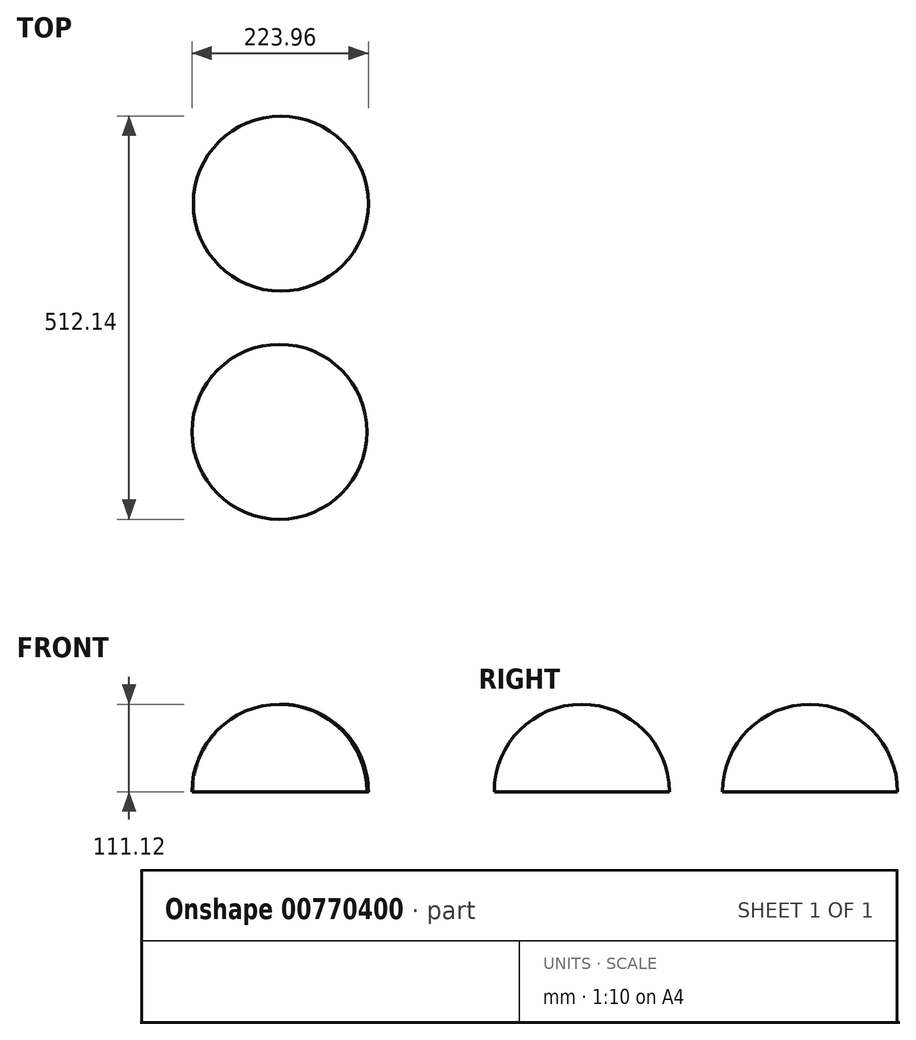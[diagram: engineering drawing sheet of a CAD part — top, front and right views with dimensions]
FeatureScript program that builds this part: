
annotation { "Feature Type Name" : "Feature", "Feature Type Description" : "" }
export const myFeature = defineFeature(function(context is Context, id is Id, definition is map)
    precondition{}
    {
        {
            var Q0;
            Q0=qCreatedBy(makeId("Top.planeOp"),FACE);
            var sketch = newSketch(context, id + "F0", { "sketchPlane" : qUnion([Q0])});
            skArc(sketch, "E0", {"start": v(7, 285.82) * mm, "mid": v(-87.3, 246.76) * mm, "end": v(-126.35, 152.47) * mm});
            skArc(sketch, "E1", {"start": v(-126.35, 152.47) * mm, "mid": v(-87.3, 58.18) * mm, "end": v(7, 19.12) * mm});
            skArc(sketch, "E2", {"start": v(7, 19.12) * mm, "mid": v(101.29, 58.18) * mm, "end": v(140.35, 152.47) * mm});
            skArc(sketch, "E3", {"start": v(140.35, 152.47) * mm, "mid": v(101.29, 246.76) * mm, "end": v(7, 285.82) * mm});
            skArc(sketch, "E4", {"start": v(7, 155.64) * mm, "mid": v(4.75, 154.71) * mm, "end": v(3.82, 152.47) * mm});
            skArc(sketch, "E5", {"start": v(3.82, 152.47) * mm, "mid": v(4.75, 150.22) * mm, "end": v(7, 149.3) * mm});
            skArc(sketch, "E6", {"start": v(7, 149.3) * mm, "mid": v(9.24, 150.22) * mm, "end": v(10.17, 152.47) * mm});
            skArc(sketch, "E7", {"start": v(10.17, 152.47) * mm, "mid": v(9.24, 154.71) * mm, "end": v(7, 155.64) * mm});
            skArc(sketch, "E8", {"start": v(5.29, -4.08) * mm, "mid": v(-89, -43.13) * mm, "end": v(-128.06, -137.43) * mm});
            skArc(sketch, "E9", {"start": v(-128.06, -137.43) * mm, "mid": v(-89, -231.72) * mm, "end": v(5.29, -270.78) * mm});
            skArc(sketch, "E10", {"start": v(5.29, -270.78) * mm, "mid": v(99.58, -231.72) * mm, "end": v(138.64, -137.43) * mm});
            skArc(sketch, "E11", {"start": v(138.64, -137.43) * mm, "mid": v(99.58, -43.13) * mm, "end": v(5.29, -4.08) * mm});
            skArc(sketch, "E12", {"start": v(5.29, -134.25) * mm, "mid": v(3.04, -135.18) * mm, "end": v(2.11, -137.43) * mm});
            skArc(sketch, "E13", {"start": v(2.11, -137.43) * mm, "mid": v(3.04, -139.67) * mm, "end": v(5.29, -140.6) * mm});
            skArc(sketch, "E14", {"start": v(5.29, -140.6) * mm, "mid": v(7.53, -139.67) * mm, "end": v(8.46, -137.43) * mm});
            skArc(sketch, "E15", {"start": v(8.46, -137.43) * mm, "mid": v(7.53, -135.18) * mm, "end": v(5.29, -134.25) * mm});
            skLineSegment(sketch, "E16", {"start": v(-168.85, -304.5) * mm, "end": v(168.85, -304.5) * mm});
            skLineSegment(sketch, "E17", {"start": v(168.85, -304.5) * mm, "end": v(168.85, 304.5) * mm});
            skLineSegment(sketch, "E18", {"start": v(168.85, 304.5) * mm, "end": v(-168.85, 304.5) * mm});
            skLineSegment(sketch, "E19", {"start": v(-168.85, 304.5) * mm, "end": v(-168.85, -304.5) * mm});
            skCircle(sketch, "E20", {"center": v(5.29, -137.43) * mm, "radius": 111.13 * mm});
            skCircle(sketch, "E21", {"center": v(7, 152.47) * mm, "radius": 111.13 * mm});
            skLineSegment(sketch, "E22", {"start": v(5.29, -270.78) * mm, "end": v(5.29, -4.08) * mm});
            skLineSegment(sketch, "E23", {"start": v(7, 19.12) * mm, "end": v(7, 285.82) * mm});
            skPoint(sketch, "E24", {"position": v(7, 41.34) * mm});
            skPoint(sketch, "E25", {"position": v(7, 263.6) * mm});
            skPoint(sketch, "E26", {"position": v(5.29, -26.3) * mm});
            skPoint(sketch, "E27", {"position": v(5.29, -248.55) * mm});
            skSolve(sketch);
        }
        {
            var Q0;
            {var subQ4=sQuery(id+"F0.wireOp",EDGE,"E14");Q0=makeQuery(id+"F0.imprint","IMPRINT",FACE,{"disambiguationData":[TD([[makeQuery(id+"F0.imprint","IMPRINT",EDGE,{"derivedFrom":subQ4}),-1.0]])]});}
            var Q1;
            {var subQ0=sQuery(id+"F0.wireOp",EDGE,"E14");Q1=makeQuery(id+"F0.imprint","IMPRINT",FACE,{"disambiguationData":[TD([[makeQuery(id+"F0.imprint","IMPRINT",EDGE,{"derivedFrom":subQ0}),1.0]])]});}
            var Q2;
            Q2=sQuery(id+"F0.wireOp",EDGE,"E22");
            revolve(context, id + "F1", {"surfaceOperationType" : NewSurfaceOperationType.NEW, "entities" : qUnion([Q0, Q1]), "axis" : qUnion([Q2]), "revolveType" : RevolveType.FULL});
        }
        {
            var Q0;
            {var subQ5=sQuery(id+"F0.wireOp",EDGE,"E4");Q0=makeQuery(id+"F0.imprint","IMPRINT",FACE,{"disambiguationData":[TD([[makeQuery(id+"F0.imprint","IMPRINT",EDGE,{"derivedFrom":subQ5}),-1.0]])]});}
            var Q1;
            {var subQ0=sQuery(id+"F0.wireOp",EDGE,"E4");Q1=makeQuery(id+"F0.imprint","IMPRINT",FACE,{"disambiguationData":[TD([[makeQuery(id+"F0.imprint","IMPRINT",EDGE,{"derivedFrom":subQ0}),1.0]])]});}
            var Q2;
            Q2=sQuery(id+"F0.wireOp",EDGE,"E23");
            revolve(context, id + "F2", {"surfaceOperationType" : NewSurfaceOperationType.NEW, "entities" : qUnion([Q0, Q1]), "axis" : qUnion([Q2]), "revolveType" : RevolveType.FULL});
        }
        {
            var Q0;
            Q0=qCreatedBy(makeId("Right.planeOp"),FACE);
            var sketch = newSketch(context, id + "F3", { "sketchPlane" : qUnion([Q0])});
            skLineSegment(sketch, "E28.bottom", {"start": v(303.55, 0) * mm, "end": v(-303.18, 0) * mm});
            skLineSegment(sketch, "E28.top", {"start": v(303.55, -134.02) * mm, "end": v(-303.18, -134.02) * mm});
            skLineSegment(sketch, "E28.left", {"start": v(303.55, 0) * mm, "end": v(303.55, -134.02) * mm});
            skLineSegment(sketch, "E28.right", {"start": v(-303.18, 0) * mm, "end": v(-303.18, -134.02) * mm});
            skSolve(sketch);
        }
        {
            var Q0;
            Q0=makeQuery(id+"F3.imprint","IMPRINT",FACE,{"disambiguationData":[TD([[makeQuery(id+"F3.imprint","IMPRINT",EDGE,{"derivedFrom":sQuery(id+"F3.wireOp",EDGE,"E28.bottom")}),1.0]])]});
            extrude(context, id + "F4", {"entities" : qUnion([Q0]), "operationType" : NewBodyOperationType.REMOVE, "oppositeDirection" : true, "depth" : 203.2 * mm, "offsetDistance" : 25.4 * mm, "hasSecondDirection" : true, "secondDirectionOppositeDirection" : false, "secondDirectionDepth" : 203.2 * mm});
        }
    });
